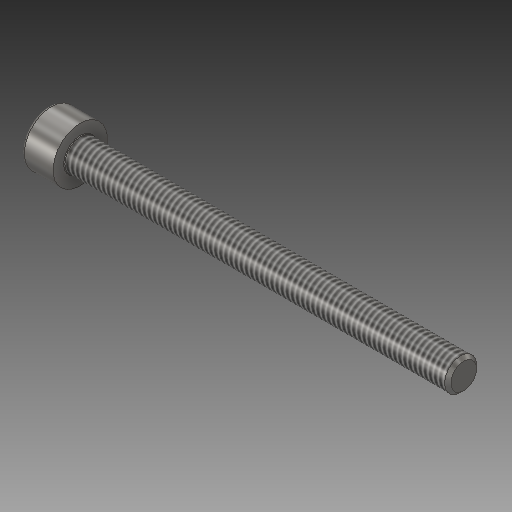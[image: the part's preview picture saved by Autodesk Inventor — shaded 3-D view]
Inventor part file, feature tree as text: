
AUTODESK INVENTOR PART (.ipt)
format: ipt  version: 2017 (Build 210142000, 142)  size: 193,536 bytes
history: native  units: mm
features: other x6, sketch x2, plane x1
ambient origin geometry x8: Origin, YZ Plane, XZ Plane, XY Plane, X Axis, Y Axis, Z Axis, Center Point
bodies: Solid1 (feature_tree)
feature tree (9):
  other  "Forged Socket Head Cap Screw - Metric M5x0.8 x 60"
  other  "Solid1::Forged Socket Head Cap Screw - Metric M5x0.8 x 60"
  other  "TaggingFeature1"
  sketch  "Sketch1"  dims[d0=10.0mm]
  sketch  "Sketch2"  dims[d19=0.0mm d28=0.0mm d29=0.0mm]
  plane  "Work Plane1"
  other  "Align 2D"
  other  "Align1"
  other  "Insert In1"
